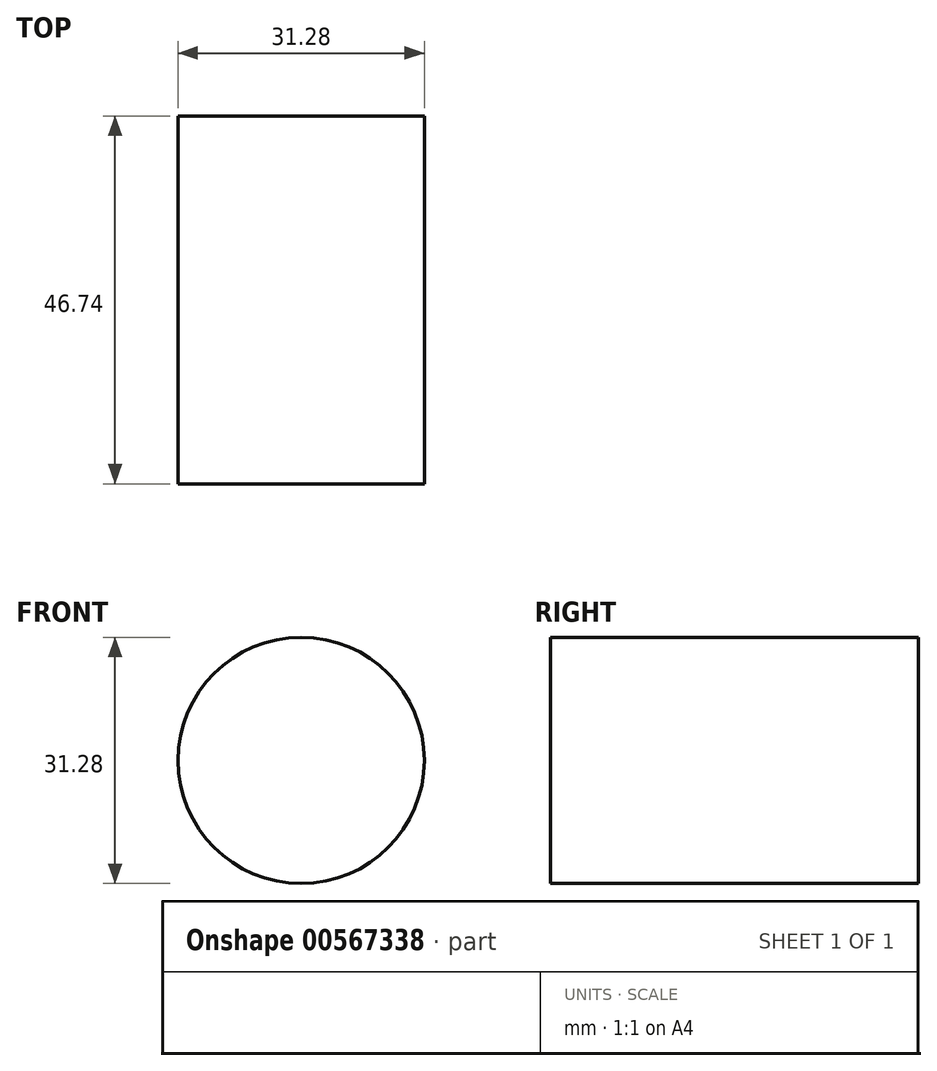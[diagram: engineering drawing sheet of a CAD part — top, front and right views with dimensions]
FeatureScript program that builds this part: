
annotation { "Feature Type Name" : "Feature", "Feature Type Description" : "" }
export const myFeature = defineFeature(function(context is Context, id is Id, definition is map)
    precondition{}
    {
        {
            var Q0;
            Q0=qCreatedBy(makeId("Front.planeOp"),FACE);
            var sketch = newSketch(context, id + "F0", { "sketchPlane" : qUnion([Q0])});
            skCircle(sketch, "E0", {"center": v(-58.58, 17.11) * mm, "radius": 15.64 * mm});
            skCircle(sketch, "E1", {"center": v(44.2, 40.12) * mm, "radius": 36.83 * mm});
            skSolve(sketch);
        }
        {
            var Q0;
            Q0=makeQuery(id+"F0.imprint","IMPRINT",FACE,{"disambiguationData":[TD([[makeQuery(id+"F0.imprint","IMPRINT",EDGE,{"derivedFrom":sQuery(id+"F0.wireOp",EDGE,"E0")}),1.0]])]});
            extrude(context, id + "F1", {"entities" : qUnion([Q0]), "depth" : 46.74 * mm, "offsetDistance" : 25.4 * mm});
        }
    });
